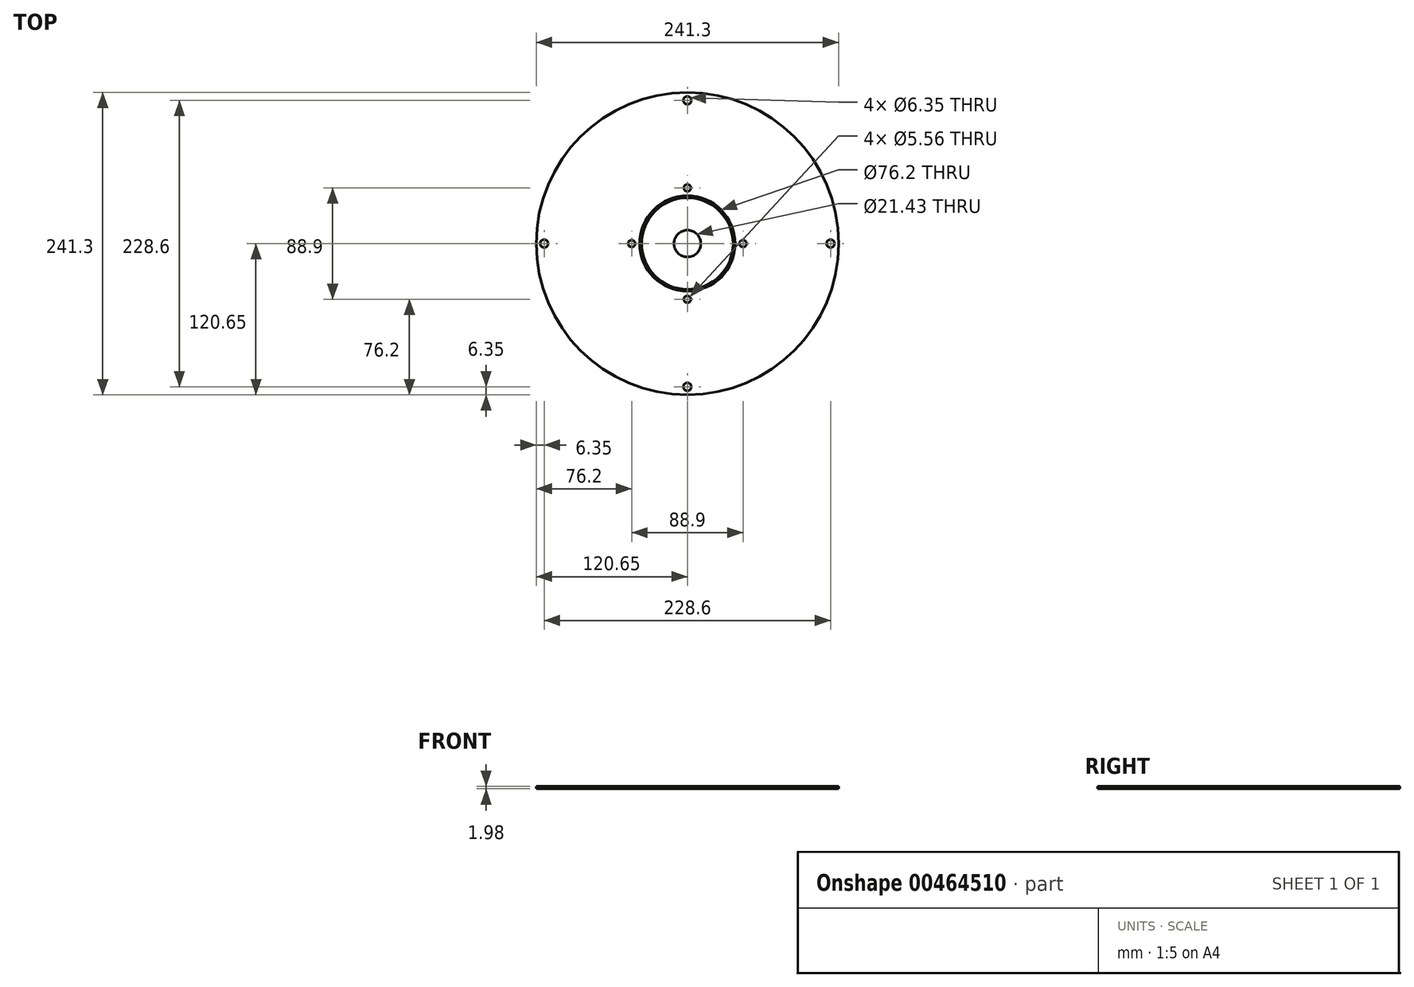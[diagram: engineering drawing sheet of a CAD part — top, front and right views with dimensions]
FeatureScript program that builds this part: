
annotation { "Feature Type Name" : "Feature", "Feature Type Description" : "" }
export const myFeature = defineFeature(function(context is Context, id is Id, definition is map)
    precondition{}
    {
        {
            var Q0;
            Q0=qCreatedBy(makeId("Top.planeOp"),FACE);
            var sketch = newSketch(context, id + "F0", { "sketchPlane" : qUnion([Q0])});
            skCircle(sketch, "E0", {"center": v(0, 0) * mm, "radius": 120.65 * mm});
            skCircle(sketch, "E1", {"center": v(0, 0) * mm, "radius": 38.1 * mm});
            skCircle(sketch, "E2", {"center": v(0, 0) * mm, "radius": 114.3 * mm, "construction": true});
            skCircle(sketch, "E3", {"center": v(0, -114.3) * mm, "radius": 3.17 * mm});
            skCircle(sketch, "E4", {"center": v(114.3, 0) * mm, "radius": 3.17 * mm});
            skCircle(sketch, "E5", {"center": v(0, 114.3) * mm, "radius": 3.17 * mm});
            skCircle(sketch, "E6", {"center": v(-114.3, 0) * mm, "radius": 3.17 * mm});
            skCircle(sketch, "E7", {"center": v(0, 44.45) * mm, "radius": 2.78 * mm});
            skCircle(sketch, "E8", {"center": v(-44.45, 0) * mm, "radius": 2.78 * mm});
            skCircle(sketch, "E9", {"center": v(0, -44.45) * mm, "radius": 2.78 * mm});
            skCircle(sketch, "E10", {"center": v(0, 0) * mm, "radius": 44.45 * mm, "construction": true});
            skCircle(sketch, "E11", {"center": v(44.45, 0) * mm, "radius": 2.78 * mm});
            skLineSegment(sketch, "E12", {"start": v(-114.3, 0) * mm, "end": v(114.3, 0) * mm, "construction": true});
            skLineSegment(sketch, "E13", {"start": v(0, -114.3) * mm, "end": v(0, 114.3) * mm, "construction": true});
            skCircle(sketch, "E14", {"center": v(0, 0) * mm, "radius": 36.51 * mm});
            skCircle(sketch, "E15", {"center": v(0, 0) * mm, "radius": 10.72 * mm});
            skSolve(sketch);
        }
        {
            var Q0;
            Q0 = qSketchRegion(id + "F0", true);
            var Q1;
            Q1=makeQuery(id+"F0.imprint","IMPRINT",FACE,{"disambiguationData":[TD([[makeQuery(id+"F0.imprint","IMPRINT",EDGE,{"derivedFrom":sQuery(id+"F0.wireOp",EDGE,"E14")}),1.0]])]});
            extrude(context, id + "F1", {"entities" : qUnion([Q0, Q1]), "depth" : 1.98 * mm});
        }
    });
